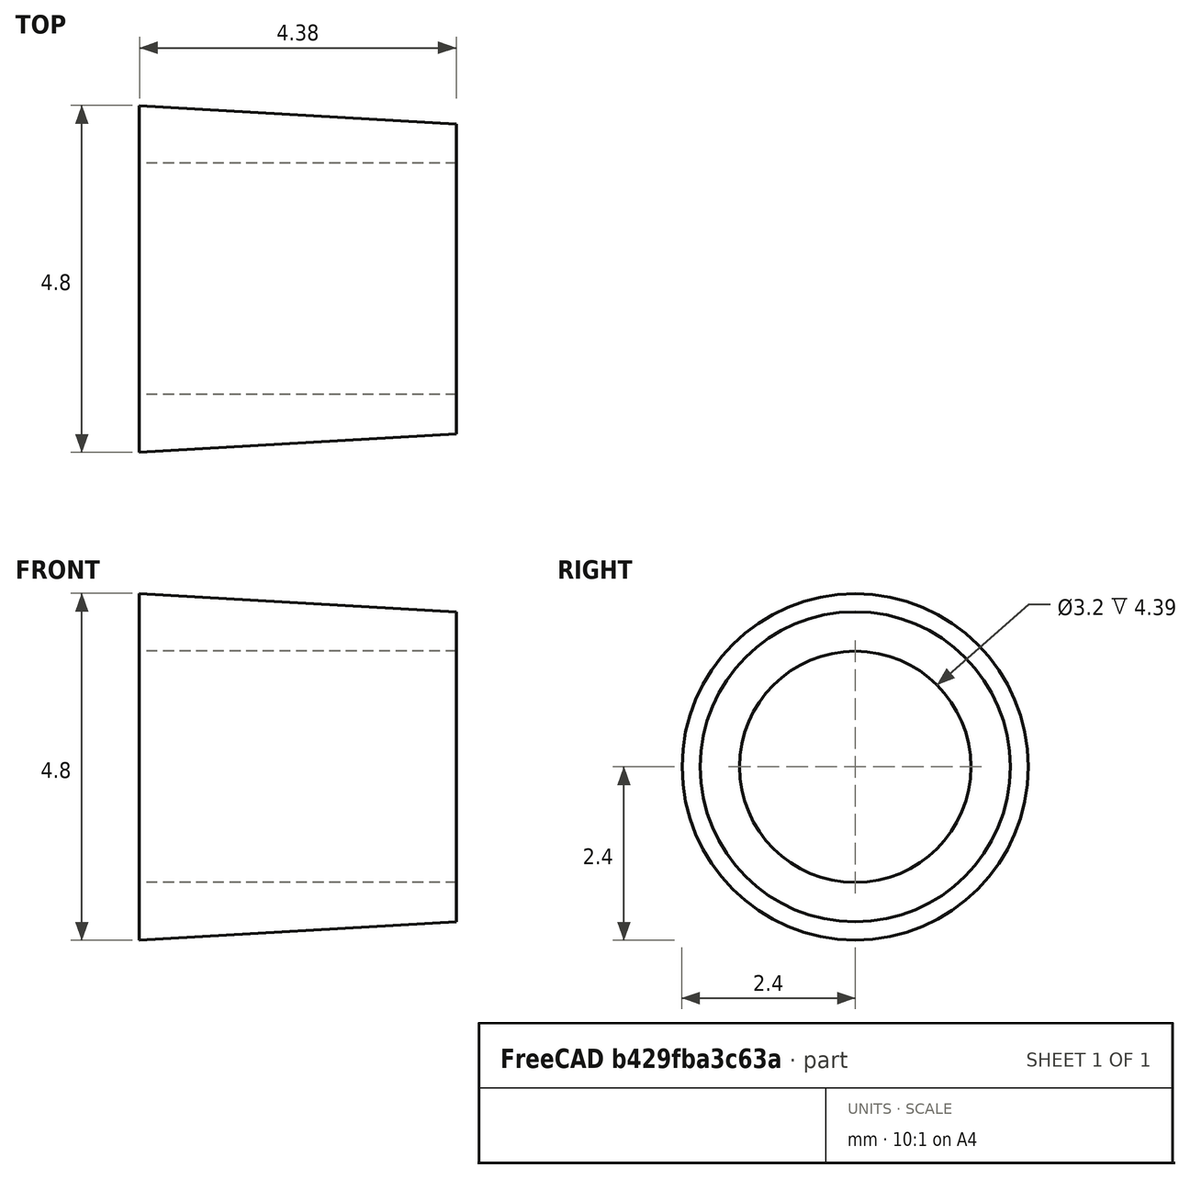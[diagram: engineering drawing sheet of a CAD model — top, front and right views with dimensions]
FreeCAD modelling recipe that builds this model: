
FCSTD DOCUMENT  (FreeCAD 0.20R29603 (Git))
Label: adaptador-eixo-amortecedor
License: All rights reserved
LicenseURL: http://en.wikipedia.org/wiki/All_rights_reserved
objects: Sketcher::SketchObject×1, PartDesign::Revolution×1, PartDesign::Body×1
note: 4 computed .brp shape members not serialized (recipe doc carries the construction recipe); baked Part::Feature solids carry a one-line shape summary decoded from their .brp

FEATURE [Sketcher::SketchObject] Sketch
  FullyConstrained = true
  MapMode = 5
  Support = -> [XY_Plane]
  sketch-geometry (6):
    g0: LineSegment StartX=0 StartY=0 StartZ=0 EndX=2.195 EndY=0 EndZ=0
    g1: LineSegment StartX=0 StartY=0 StartZ=0 EndX=-2.195 EndY=0 EndZ=0
    g2: LineSegment StartX=2.195 StartY=1.6 StartZ=0 EndX=-2.195 EndY=1.6 EndZ=0
    g3: LineSegment StartX=-2.195 StartY=1.6 StartZ=0 EndX=-2.195 EndY=2.395 EndZ=0
    g4: LineSegment StartX=-2.195 StartY=2.395 StartZ=0 EndX=2.195 EndY=2.145 EndZ=0
    g5: LineSegment StartX=2.195 StartY=2.145 StartZ=0 EndX=2.195 EndY=1.6 EndZ=0
  constraints (18):
    c: Coincident(g0,g-1)
    c: PointOnObject(g0,g-1)
    c: Coincident(g1,g0)
    c: PointOnObject(g1,g-1)
    c: Equal(g1,g0)
    c: Horizontal(g2)
    c: Coincident(g2,g3)
    c: Vertical(g3)
    c: Coincident(g3,g4)
    c: Coincident(g4,g5)
    c: Coincident(g5,g2)
    c: Vertical(g5)
    c: DistanceY(g0,g2) = 1.6
    c: Vertical(g0,g2)
    c: Vertical(g1,g2)
    c: DistanceY(g1,g3) = 2.395
    c: DistanceY(g0,g4) = 2.145
    c: DistanceX(g2,g2) = 4.39
FEATURE [PartDesign::Revolution] Revolution
  Angle = 360
  Axis = (1,0,0)
  Base = (0,0,0)
  Profile = -> Sketch
  ReferenceAxis = -> Sketch [H_Axis]
FEATURE [PartDesign::Body] Body
  Group = -> [Sketch,Revolution]
  Origin = -> Origin
  Tip = -> Revolution
